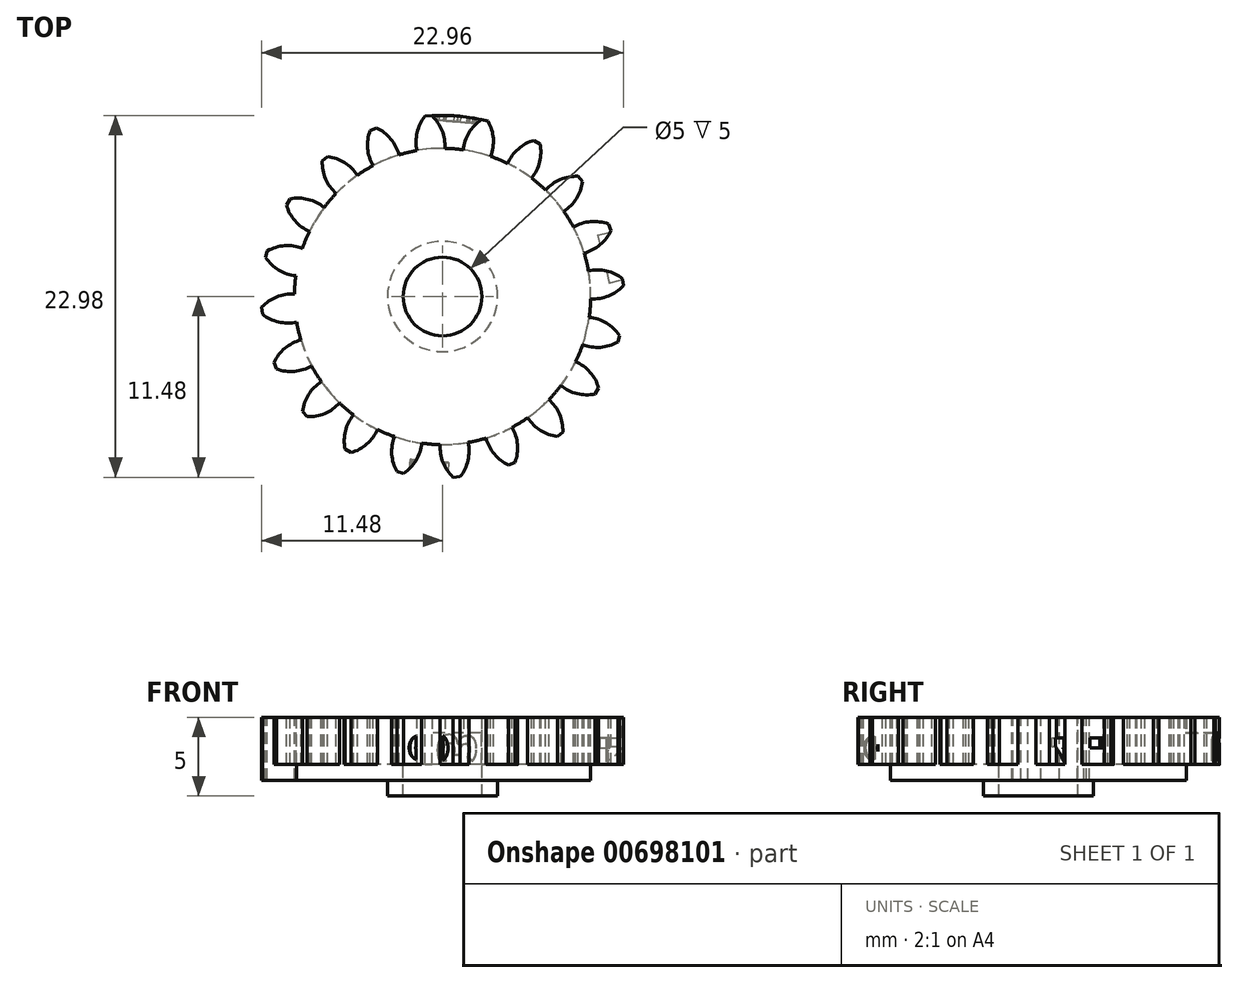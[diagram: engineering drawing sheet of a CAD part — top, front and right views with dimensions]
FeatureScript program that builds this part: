
annotation { "Feature Type Name" : "Feature", "Feature Type Description" : "" }
export const myFeature = defineFeature(function(context is Context, id is Id, definition is map)
    precondition{}
    {
        {
            assignVariable(context, id + "F0", {"name" : "GearDepth", "anyValue" : 1});
        }
        {
            var Q0;
            Q0=qCreatedBy(makeId("Top.planeOp"),FACE);
            var sketch = newSketch(context, id + "F1", { "sketchPlane" : qUnion([Q0])});
            skCircle(sketch, "E0", {"center": v(0, 0) * mm, "radius": 9.4 * mm});
            skCircle(sketch, "E1", {"center": v(0, 0) * mm, "radius": 10.45 * mm, "construction": true});
            skCircle(sketch, "E2", {"center": v(0, 0) * mm, "radius": 11.5 * mm});
            skLineSegment(sketch, "E3", {"start": v(0, 0) * mm, "end": v(0, 17.6) * mm, "construction": true});
            skLineSegment(sketch, "E4", {"start": v(0, 0) * mm, "end": v(-1.42, 18) * mm, "construction": true});
            skLineSegment(sketch, "E5", {"start": v(0, 10.45) * mm, "end": v(-10.54, 10.45) * mm, "construction": true});
            skLineSegment(sketch, "E6", {"start": v(0, 10.45) * mm, "end": v(-10.3, 6.7) * mm, "construction": true});
            skCircle(sketch, "E7", {"center": v(0, 10.45) * mm, "radius": 2.61 * mm, "construction": true});
            skCircle(sketch, "E8", {"center": v(-2.46, 9.56) * mm, "radius": 2.61 * mm, "construction": true});
            skArc(sketch, "E9", {"start": v(-4.91, 10.45) * mm, "mid": v(-4.92, 10.42) * mm, "end": v(-4.94, 10.39) * mm});
            skArc(sketch, "E10.trimOffspring", {"start": v(0.15, 9.4) * mm, "mid": v(-0.03, 10.54) * mm, "end": v(-0.68, 11.48) * mm});
            skArc(sketch, "E11.MirrorCS", {"start": v(-1.62, 9.27) * mm, "mid": v(-1.62, 10.41) * mm, "end": v(-1.12, 11.45) * mm});
            skLineSegment(sketch, "E12", {"start": v(-1.12, 11.45) * mm, "end": v(-0.68, 11.48) * mm});
            skArc(sketch, "E13.1.0", {"start": v(-2.76, 9) * mm, "mid": v(-3.29, 10.01) * mm, "end": v(-4.2, 10.7) * mm});
            skLineSegment(sketch, "E13.1.1", {"start": v(-4.6, 10.54) * mm, "end": v(-4.2, 10.7) * mm});
            skArc(sketch, "E13.1.2", {"start": v(-4.4, 8.31) * mm, "mid": v(-4.76, 9.4) * mm, "end": v(-4.6, 10.54) * mm});
            skArc(sketch, "E13.2.0", {"start": v(-5.4, 7.7) * mm, "mid": v(-6.22, 8.5) * mm, "end": v(-7.3, 8.89) * mm});
            skLineSegment(sketch, "E13.2.1", {"start": v(-7.64, 8.6) * mm, "end": v(-7.3, 8.89) * mm});
            skArc(sketch, "E13.2.2", {"start": v(-6.76, 6.54) * mm, "mid": v(-7.43, 7.47) * mm, "end": v(-7.64, 8.6) * mm});
            skArc(sketch, "E13.3.0", {"start": v(-7.52, 5.65) * mm, "mid": v(-8.54, 6.17) * mm, "end": v(-9.69, 6.2) * mm});
            skLineSegment(sketch, "E13.3.1", {"start": v(-9.92, 5.82) * mm, "end": v(-9.69, 6.2) * mm});
            skArc(sketch, "E13.3.2", {"start": v(-8.45, 4.13) * mm, "mid": v(-9.37, 4.81) * mm, "end": v(-9.92, 5.82) * mm});
            skArc(sketch, "E13.4.0", {"start": v(-8.9, 3.05) * mm, "mid": v(-10.03, 3.23) * mm, "end": v(-11.13, 2.9) * mm});
            skLineSegment(sketch, "E13.4.1", {"start": v(-11.23, 2.47) * mm, "end": v(-11.13, 2.9) * mm});
            skArc(sketch, "E13.4.2", {"start": v(-9.32, 1.32) * mm, "mid": v(-10.4, 1.68) * mm, "end": v(-11.23, 2.47) * mm});
            skArc(sketch, "E13.5.0", {"start": v(-9.4, 0.15) * mm, "mid": v(-10.54, -0.03) * mm, "end": v(-11.48, -0.68) * mm});
            skLineSegment(sketch, "E13.5.1", {"start": v(-11.45, -1.12) * mm, "end": v(-11.48, -0.68) * mm});
            skArc(sketch, "E13.5.2", {"start": v(-9.27, -1.62) * mm, "mid": v(-10.41, -1.62) * mm, "end": v(-11.45, -1.12) * mm});
            skArc(sketch, "E13.6.0", {"start": v(-9, -2.76) * mm, "mid": v(-10.01, -3.29) * mm, "end": v(-10.7, -4.2) * mm});
            skLineSegment(sketch, "E13.6.1", {"start": v(-10.54, -4.6) * mm, "end": v(-10.7, -4.2) * mm});
            skArc(sketch, "E13.6.2", {"start": v(-8.31, -4.4) * mm, "mid": v(-9.4, -4.76) * mm, "end": v(-10.54, -4.6) * mm});
            skArc(sketch, "E13.7.0", {"start": v(-7.7, -5.4) * mm, "mid": v(-8.5, -6.22) * mm, "end": v(-8.89, -7.3) * mm});
            skLineSegment(sketch, "E13.7.1", {"start": v(-8.6, -7.64) * mm, "end": v(-8.89, -7.3) * mm});
            skArc(sketch, "E13.7.2", {"start": v(-6.54, -6.76) * mm, "mid": v(-7.47, -7.43) * mm, "end": v(-8.6, -7.64) * mm});
            skArc(sketch, "E13.8.0", {"start": v(-5.65, -7.52) * mm, "mid": v(-6.17, -8.54) * mm, "end": v(-6.2, -9.69) * mm});
            skLineSegment(sketch, "E13.8.1", {"start": v(-5.82, -9.92) * mm, "end": v(-6.2, -9.69) * mm});
            skArc(sketch, "E13.8.2", {"start": v(-4.13, -8.45) * mm, "mid": v(-4.81, -9.37) * mm, "end": v(-5.82, -9.92) * mm});
            skArc(sketch, "E13.9.0", {"start": v(-3.05, -8.9) * mm, "mid": v(-3.23, -10.03) * mm, "end": v(-2.9, -11.13) * mm});
            skLineSegment(sketch, "E13.9.1", {"start": v(-2.47, -11.23) * mm, "end": v(-2.9, -11.13) * mm});
            skArc(sketch, "E13.9.2", {"start": v(-1.32, -9.32) * mm, "mid": v(-1.68, -10.4) * mm, "end": v(-2.47, -11.23) * mm});
            skArc(sketch, "E13.10.0", {"start": v(-0.15, -9.4) * mm, "mid": v(0.03, -10.54) * mm, "end": v(0.68, -11.48) * mm});
            skLineSegment(sketch, "E13.10.1", {"start": v(1.12, -11.45) * mm, "end": v(0.68, -11.48) * mm});
            skArc(sketch, "E13.10.2", {"start": v(1.62, -9.27) * mm, "mid": v(1.62, -10.41) * mm, "end": v(1.12, -11.45) * mm});
            skArc(sketch, "E13.11.0", {"start": v(2.76, -9) * mm, "mid": v(3.29, -10.01) * mm, "end": v(4.2, -10.7) * mm});
            skLineSegment(sketch, "E13.11.1", {"start": v(4.6, -10.54) * mm, "end": v(4.2, -10.7) * mm});
            skArc(sketch, "E13.11.2", {"start": v(4.4, -8.31) * mm, "mid": v(4.76, -9.4) * mm, "end": v(4.6, -10.54) * mm});
            skArc(sketch, "E13.12.0", {"start": v(5.4, -7.7) * mm, "mid": v(6.22, -8.5) * mm, "end": v(7.3, -8.89) * mm});
            skLineSegment(sketch, "E13.12.1", {"start": v(7.64, -8.6) * mm, "end": v(7.3, -8.89) * mm});
            skArc(sketch, "E13.12.2", {"start": v(6.76, -6.54) * mm, "mid": v(7.43, -7.47) * mm, "end": v(7.64, -8.6) * mm});
            skArc(sketch, "E13.13.0", {"start": v(7.52, -5.65) * mm, "mid": v(8.54, -6.17) * mm, "end": v(9.69, -6.2) * mm});
            skLineSegment(sketch, "E13.13.1", {"start": v(9.92, -5.82) * mm, "end": v(9.69, -6.2) * mm});
            skArc(sketch, "E13.13.2", {"start": v(8.45, -4.13) * mm, "mid": v(9.37, -4.81) * mm, "end": v(9.92, -5.82) * mm});
            skArc(sketch, "E13.14.0", {"start": v(8.9, -3.05) * mm, "mid": v(10.03, -3.23) * mm, "end": v(11.13, -2.9) * mm});
            skLineSegment(sketch, "E13.14.1", {"start": v(11.23, -2.47) * mm, "end": v(11.13, -2.9) * mm});
            skArc(sketch, "E13.14.2", {"start": v(9.32, -1.32) * mm, "mid": v(10.4, -1.68) * mm, "end": v(11.23, -2.47) * mm});
            skArc(sketch, "E13.15.0", {"start": v(9.4, -0.15) * mm, "mid": v(10.54, 0.03) * mm, "end": v(11.48, 0.68) * mm});
            skLineSegment(sketch, "E13.15.1", {"start": v(11.45, 1.12) * mm, "end": v(11.48, 0.68) * mm});
            skArc(sketch, "E13.15.2", {"start": v(9.27, 1.62) * mm, "mid": v(10.41, 1.62) * mm, "end": v(11.45, 1.12) * mm});
            skArc(sketch, "E13.16.0", {"start": v(9, 2.76) * mm, "mid": v(10.01, 3.29) * mm, "end": v(10.7, 4.2) * mm});
            skLineSegment(sketch, "E13.16.1", {"start": v(10.54, 4.6) * mm, "end": v(10.7, 4.2) * mm});
            skArc(sketch, "E13.16.2", {"start": v(8.31, 4.4) * mm, "mid": v(9.4, 4.76) * mm, "end": v(10.54, 4.6) * mm});
            skArc(sketch, "E13.17.0", {"start": v(7.7, 5.4) * mm, "mid": v(8.5, 6.22) * mm, "end": v(8.89, 7.3) * mm});
            skLineSegment(sketch, "E13.17.1", {"start": v(8.6, 7.64) * mm, "end": v(8.89, 7.3) * mm});
            skArc(sketch, "E13.17.2", {"start": v(6.54, 6.76) * mm, "mid": v(7.47, 7.43) * mm, "end": v(8.6, 7.64) * mm});
            skArc(sketch, "E13.18.0", {"start": v(5.65, 7.52) * mm, "mid": v(6.17, 8.54) * mm, "end": v(6.2, 9.69) * mm});
            skLineSegment(sketch, "E13.18.1", {"start": v(5.82, 9.92) * mm, "end": v(6.2, 9.69) * mm});
            skArc(sketch, "E13.18.2", {"start": v(4.13, 8.45) * mm, "mid": v(4.81, 9.37) * mm, "end": v(5.82, 9.92) * mm});
            skArc(sketch, "E13.19.0", {"start": v(3.05, 8.9) * mm, "mid": v(3.23, 10.03) * mm, "end": v(2.9, 11.13) * mm});
            skLineSegment(sketch, "E13.19.1", {"start": v(2.47, 11.23) * mm, "end": v(2.9, 11.13) * mm});
            skArc(sketch, "E13.19.2", {"start": v(1.32, 9.32) * mm, "mid": v(1.68, 10.4) * mm, "end": v(2.47, 11.23) * mm});
            skCircle(sketch, "E14", {"center": v(0, 0) * mm, "radius": 2.5 * mm});
            skCircle(sketch, "E15", {"center": v(0, 0) * mm, "radius": 3.5 * mm});
            skPoint(sketch, "E16", {"position": v(-11.47, 0.86) * mm});
            skSolve(sketch);
        }
        {
            var Q0;
            {var subQ0=sQuery(id+"F1.wireOp",EDGE,"E13.5.0");Q0=makeQuery(id+"F1.imprint","IMPRINT",FACE,{"disambiguationData":[TD([[makeQuery(id+"F1.imprint","IMPRINT",EDGE,{"derivedFrom":subQ0}),1.0]])]});}
            var Q1;
            {var subQ0=sQuery(id+"F1.wireOp",EDGE,"E13.4.0");Q1=makeQuery(id+"F1.imprint","IMPRINT",FACE,{"disambiguationData":[TD([[makeQuery(id+"F1.imprint","IMPRINT",EDGE,{"derivedFrom":subQ0}),1.0]])]});}
            var Q2;
            Q2=makeQuery(id+"F1.imprint","IMPRINT",FACE,{"disambiguationData":[TD([[makeQuery(id+"F1.imprint","IMPRINT",EDGE,{"derivedFrom":sQuery(id+"F1.wireOp",EDGE,"E14")}),-1.0]])]});
            var Q3;
            Q3=makeQuery(id+"F1.imprint","IMPRINT",FACE,{"disambiguationData":[TD([[makeQuery(id+"F1.imprint","IMPRINT",EDGE,{"derivedFrom":sQuery(id+"F1.wireOp",EDGE,"E15")}),-1.0]])]});
            extrude(context, id + "F2", {"entities" : qUnion([Q0, Q1, Q2, Q3]), "oppositeDirection" : true, "depth" : 3 * mm});
        }
        {
            var Q0;
            Q0=makeQuery(id+"F1.imprint","IMPRINT",FACE,{"disambiguationData":[TD([[makeQuery(id+"F1.imprint","IMPRINT",EDGE,{"derivedFrom":sQuery(id+"F1.wireOp",EDGE,"E14")}),-1.0]])]});
            var Q1;
            {var subQ0=sQuery(id+"F1.wireOp",EDGE,"E13.10.2");Q1=makeQuery(id+"F1.imprint","IMPRINT",FACE,{"disambiguationData":[TD([[makeQuery(id+"F1.imprint","IMPRINT",EDGE,{"derivedFrom":subQ0}),1.0]])]});}
            var Q2;
            {var subQ0=sQuery(id+"F1.wireOp",EDGE,"E13.11.0");Q2=makeQuery(id+"F1.imprint","IMPRINT",FACE,{"disambiguationData":[TD([[makeQuery(id+"F1.imprint","IMPRINT",EDGE,{"derivedFrom":subQ0}),1.0]])]});}
            var Q3;
            {var subQ0=sQuery(id+"F1.wireOp",EDGE,"E13.11.2");Q3=makeQuery(id+"F1.imprint","IMPRINT",FACE,{"disambiguationData":[TD([[makeQuery(id+"F1.imprint","IMPRINT",EDGE,{"derivedFrom":subQ0}),1.0]])]});}
            var Q4;
            {var subQ0=sQuery(id+"F1.wireOp",EDGE,"E13.12.0");Q4=makeQuery(id+"F1.imprint","IMPRINT",FACE,{"disambiguationData":[TD([[makeQuery(id+"F1.imprint","IMPRINT",EDGE,{"derivedFrom":subQ0}),1.0]])]});}
            var Q5;
            {var subQ0=sQuery(id+"F1.wireOp",EDGE,"E13.12.2");Q5=makeQuery(id+"F1.imprint","IMPRINT",FACE,{"disambiguationData":[TD([[makeQuery(id+"F1.imprint","IMPRINT",EDGE,{"derivedFrom":subQ0}),1.0]])]});}
            var Q6;
            {var subQ0=sQuery(id+"F1.wireOp",EDGE,"E13.13.0");Q6=makeQuery(id+"F1.imprint","IMPRINT",FACE,{"disambiguationData":[TD([[makeQuery(id+"F1.imprint","IMPRINT",EDGE,{"derivedFrom":subQ0}),1.0]])]});}
            var Q7;
            {var subQ0=sQuery(id+"F1.wireOp",EDGE,"E13.13.2");Q7=makeQuery(id+"F1.imprint","IMPRINT",FACE,{"disambiguationData":[TD([[makeQuery(id+"F1.imprint","IMPRINT",EDGE,{"derivedFrom":subQ0}),1.0]])]});}
            var Q8;
            {var subQ0=sQuery(id+"F1.wireOp",EDGE,"E13.14.0");Q8=makeQuery(id+"F1.imprint","IMPRINT",FACE,{"disambiguationData":[TD([[makeQuery(id+"F1.imprint","IMPRINT",EDGE,{"derivedFrom":subQ0}),1.0]])]});}
            var Q9;
            {var subQ0=sQuery(id+"F1.wireOp",EDGE,"E13.14.2");Q9=makeQuery(id+"F1.imprint","IMPRINT",FACE,{"disambiguationData":[TD([[makeQuery(id+"F1.imprint","IMPRINT",EDGE,{"derivedFrom":subQ0}),1.0]])]});}
            var Q10;
            {var subQ0=sQuery(id+"F1.wireOp",EDGE,"E13.15.0");Q10=makeQuery(id+"F1.imprint","IMPRINT",FACE,{"disambiguationData":[TD([[makeQuery(id+"F1.imprint","IMPRINT",EDGE,{"derivedFrom":subQ0}),1.0]])]});}
            var Q11;
            {var subQ0=sQuery(id+"F1.wireOp",EDGE,"E13.15.2");Q11=makeQuery(id+"F1.imprint","IMPRINT",FACE,{"disambiguationData":[TD([[makeQuery(id+"F1.imprint","IMPRINT",EDGE,{"derivedFrom":subQ0}),1.0]])]});}
            var Q12;
            {var subQ0=sQuery(id+"F1.wireOp",EDGE,"E13.16.0");Q12=makeQuery(id+"F1.imprint","IMPRINT",FACE,{"disambiguationData":[TD([[makeQuery(id+"F1.imprint","IMPRINT",EDGE,{"derivedFrom":subQ0}),1.0]])]});}
            var Q13;
            {var subQ0=sQuery(id+"F1.wireOp",EDGE,"E13.16.2");Q13=makeQuery(id+"F1.imprint","IMPRINT",FACE,{"disambiguationData":[TD([[makeQuery(id+"F1.imprint","IMPRINT",EDGE,{"derivedFrom":subQ0}),1.0]])]});}
            var Q14;
            {var subQ0=sQuery(id+"F1.wireOp",EDGE,"E13.17.0");Q14=makeQuery(id+"F1.imprint","IMPRINT",FACE,{"disambiguationData":[TD([[makeQuery(id+"F1.imprint","IMPRINT",EDGE,{"derivedFrom":subQ0}),1.0]])]});}
            var Q15;
            {var subQ0=sQuery(id+"F1.wireOp",EDGE,"E13.17.2");Q15=makeQuery(id+"F1.imprint","IMPRINT",FACE,{"disambiguationData":[TD([[makeQuery(id+"F1.imprint","IMPRINT",EDGE,{"derivedFrom":subQ0}),1.0]])]});}
            var Q16;
            {var subQ0=sQuery(id+"F1.wireOp",EDGE,"E13.18.0");Q16=makeQuery(id+"F1.imprint","IMPRINT",FACE,{"disambiguationData":[TD([[makeQuery(id+"F1.imprint","IMPRINT",EDGE,{"derivedFrom":subQ0}),1.0]])]});}
            var Q17;
            {var subQ0=sQuery(id+"F1.wireOp",EDGE,"E13.18.2");Q17=makeQuery(id+"F1.imprint","IMPRINT",FACE,{"disambiguationData":[TD([[makeQuery(id+"F1.imprint","IMPRINT",EDGE,{"derivedFrom":subQ0}),1.0]])]});}
            var Q18;
            {var subQ0=sQuery(id+"F1.wireOp",EDGE,"E13.19.0");Q18=makeQuery(id+"F1.imprint","IMPRINT",FACE,{"disambiguationData":[TD([[makeQuery(id+"F1.imprint","IMPRINT",EDGE,{"derivedFrom":subQ0}),1.0]])]});}
            var Q19;
            {var subQ0=sQuery(id+"F1.wireOp",EDGE,"E10.trimOffspring");Q19=makeQuery(id+"F1.imprint","IMPRINT",FACE,{"disambiguationData":[TD([[makeQuery(id+"F1.imprint","IMPRINT",EDGE,{"derivedFrom":subQ0}),-1.0]])]});}
            var Q20;
            {var subQ0=sQuery(id+"F1.wireOp",EDGE,"E10.trimOffspring");Q20=makeQuery(id+"F1.imprint","IMPRINT",FACE,{"disambiguationData":[TD([[makeQuery(id+"F1.imprint","IMPRINT",EDGE,{"derivedFrom":subQ0}),1.0]])]});}
            var Q21;
            {var subQ0=sQuery(id+"F1.wireOp",EDGE,"E11.MirrorCS");Q21=makeQuery(id+"F1.imprint","IMPRINT",FACE,{"disambiguationData":[TD([[makeQuery(id+"F1.imprint","IMPRINT",EDGE,{"derivedFrom":subQ0}),1.0]])]});}
            var Q22;
            {var subQ0=sQuery(id+"F1.wireOp",EDGE,"E13.1.0");Q22=makeQuery(id+"F1.imprint","IMPRINT",FACE,{"disambiguationData":[TD([[makeQuery(id+"F1.imprint","IMPRINT",EDGE,{"derivedFrom":subQ0}),1.0]])]});}
            var Q23;
            {var subQ0=sQuery(id+"F1.wireOp",EDGE,"E13.1.2");Q23=makeQuery(id+"F1.imprint","IMPRINT",FACE,{"disambiguationData":[TD([[makeQuery(id+"F1.imprint","IMPRINT",EDGE,{"derivedFrom":subQ0}),1.0]])]});}
            var Q24;
            {var subQ0=sQuery(id+"F1.wireOp",EDGE,"E13.2.0");Q24=makeQuery(id+"F1.imprint","IMPRINT",FACE,{"disambiguationData":[TD([[makeQuery(id+"F1.imprint","IMPRINT",EDGE,{"derivedFrom":subQ0}),1.0]])]});}
            var Q25;
            {var subQ0=sQuery(id+"F1.wireOp",EDGE,"E13.2.2");Q25=makeQuery(id+"F1.imprint","IMPRINT",FACE,{"disambiguationData":[TD([[makeQuery(id+"F1.imprint","IMPRINT",EDGE,{"derivedFrom":subQ0}),1.0]])]});}
            var Q26;
            {var subQ0=sQuery(id+"F1.wireOp",EDGE,"E13.3.0");Q26=makeQuery(id+"F1.imprint","IMPRINT",FACE,{"disambiguationData":[TD([[makeQuery(id+"F1.imprint","IMPRINT",EDGE,{"derivedFrom":subQ0}),1.0]])]});}
            var Q27;
            {var subQ0=sQuery(id+"F1.wireOp",EDGE,"E13.3.2");Q27=makeQuery(id+"F1.imprint","IMPRINT",FACE,{"disambiguationData":[TD([[makeQuery(id+"F1.imprint","IMPRINT",EDGE,{"derivedFrom":subQ0}),1.0]])]});}
            var Q28;
            {var subQ0=sQuery(id+"F1.wireOp",EDGE,"E13.4.0");Q28=makeQuery(id+"F1.imprint","IMPRINT",FACE,{"disambiguationData":[TD([[makeQuery(id+"F1.imprint","IMPRINT",EDGE,{"derivedFrom":subQ0}),1.0]])]});}
            var Q29;
            {var subQ0=sQuery(id+"F1.wireOp",EDGE,"E13.4.2");Q29=makeQuery(id+"F1.imprint","IMPRINT",FACE,{"disambiguationData":[TD([[makeQuery(id+"F1.imprint","IMPRINT",EDGE,{"derivedFrom":subQ0}),1.0]])]});}
            var Q30;
            {var subQ0=sQuery(id+"F1.wireOp",EDGE,"E13.5.0");Q30=makeQuery(id+"F1.imprint","IMPRINT",FACE,{"disambiguationData":[TD([[makeQuery(id+"F1.imprint","IMPRINT",EDGE,{"derivedFrom":subQ0}),1.0]])]});}
            var Q31;
            {var subQ0=sQuery(id+"F1.wireOp",EDGE,"E13.5.2");Q31=makeQuery(id+"F1.imprint","IMPRINT",FACE,{"disambiguationData":[TD([[makeQuery(id+"F1.imprint","IMPRINT",EDGE,{"derivedFrom":subQ0}),1.0]])]});}
            var Q32;
            {var subQ0=sQuery(id+"F1.wireOp",EDGE,"E13.6.0");Q32=makeQuery(id+"F1.imprint","IMPRINT",FACE,{"disambiguationData":[TD([[makeQuery(id+"F1.imprint","IMPRINT",EDGE,{"derivedFrom":subQ0}),1.0]])]});}
            var Q33;
            {var subQ0=sQuery(id+"F1.wireOp",EDGE,"E13.6.2");Q33=makeQuery(id+"F1.imprint","IMPRINT",FACE,{"disambiguationData":[TD([[makeQuery(id+"F1.imprint","IMPRINT",EDGE,{"derivedFrom":subQ0}),1.0]])]});}
            var Q34;
            {var subQ0=sQuery(id+"F1.wireOp",EDGE,"E13.7.0");Q34=makeQuery(id+"F1.imprint","IMPRINT",FACE,{"disambiguationData":[TD([[makeQuery(id+"F1.imprint","IMPRINT",EDGE,{"derivedFrom":subQ0}),1.0]])]});}
            var Q35;
            {var subQ0=sQuery(id+"F1.wireOp",EDGE,"E13.7.2");Q35=makeQuery(id+"F1.imprint","IMPRINT",FACE,{"disambiguationData":[TD([[makeQuery(id+"F1.imprint","IMPRINT",EDGE,{"derivedFrom":subQ0}),1.0]])]});}
            var Q36;
            {var subQ0=sQuery(id+"F1.wireOp",EDGE,"E13.8.0");Q36=makeQuery(id+"F1.imprint","IMPRINT",FACE,{"disambiguationData":[TD([[makeQuery(id+"F1.imprint","IMPRINT",EDGE,{"derivedFrom":subQ0}),1.0]])]});}
            var Q37;
            {var subQ0=sQuery(id+"F1.wireOp",EDGE,"E13.8.2");Q37=makeQuery(id+"F1.imprint","IMPRINT",FACE,{"disambiguationData":[TD([[makeQuery(id+"F1.imprint","IMPRINT",EDGE,{"derivedFrom":subQ0}),1.0]])]});}
            var Q38;
            {var subQ0=sQuery(id+"F1.wireOp",EDGE,"E13.9.0");Q38=makeQuery(id+"F1.imprint","IMPRINT",FACE,{"disambiguationData":[TD([[makeQuery(id+"F1.imprint","IMPRINT",EDGE,{"derivedFrom":subQ0}),1.0]])]});}
            var Q39;
            {var subQ0=sQuery(id+"F1.wireOp",EDGE,"E13.9.2");Q39=makeQuery(id+"F1.imprint","IMPRINT",FACE,{"disambiguationData":[TD([[makeQuery(id+"F1.imprint","IMPRINT",EDGE,{"derivedFrom":subQ0}),1.0]])]});}
            var Q40;
            {var subQ0=sQuery(id+"F1.wireOp",EDGE,"E13.10.0");Q40=makeQuery(id+"F1.imprint","IMPRINT",FACE,{"disambiguationData":[TD([[makeQuery(id+"F1.imprint","IMPRINT",EDGE,{"derivedFrom":subQ0}),1.0]])]});}
            var Q41;
            Q41=makeQuery(id+"F1.imprint","IMPRINT",FACE,{"disambiguationData":[TD([[makeQuery(id+"F1.imprint","IMPRINT",EDGE,{"derivedFrom":sQuery(id+"F1.wireOp",EDGE,"E15")}),-1.0]])]});
            extrude(context, id + "F3", {"entities" : qUnion([Q0, Q1, Q2, Q3, Q4, Q5, Q6, Q7, Q8, Q9, Q10, Q11, Q12, Q13, Q14, Q15, Q16, Q17, Q18, Q19, Q20, Q21, Q22, Q23, Q24, Q25, Q26, Q27, Q28, Q29, Q30, Q31, Q32, Q33, Q34, Q35, Q36, Q37, Q38, Q39, Q40, Q41]), "operationType" : NewBodyOperationType.ADD, "oppositeDirection" : true, "depth" : 2 * mm});
        }
        {
            var Q0;
            {var subQ0=sQuery(id+"F1.wireOp",EDGE,"E10.trimOffspring");Q0=makeQuery(id+"F1.imprint","IMPRINT",FACE,{"disambiguationData":[TD([[makeQuery(id+"F1.imprint","IMPRINT",EDGE,{"derivedFrom":subQ0}),1.0]])]});}
            var Q1;
            {var subQ0=sQuery(id+"F1.wireOp",EDGE,"E0");var subQ1=makeQuery(id+"F1.imprint","INTERSECT",VERTEX,{"derivedFrom":[subQ0,sQuery(id+"F1.wireOp",EDGE,"E10.trimOffspring")]});Q1=makeQuery(id+"F1.imprint","IMPRINT",FACE,{"disambiguationData":[TD([[makeQuery(id+"F1.imprint","IMPRINT",EDGE,{"disambiguationData":[TD([[subQ1,-1.0]])],"derivedFrom":subQ0}),1.0]])]});}
            var Q2;
            {var subQ0=sQuery(id+"F1.wireOp",EDGE,"E13.1.0");Q2=makeQuery(id+"F1.imprint","IMPRINT",FACE,{"disambiguationData":[TD([[makeQuery(id+"F1.imprint","IMPRINT",EDGE,{"derivedFrom":subQ0}),1.0]])]});}
            var Q3;
            {var subQ0=sQuery(id+"F1.wireOp",EDGE,"E13.2.0");Q3=makeQuery(id+"F1.imprint","IMPRINT",FACE,{"disambiguationData":[TD([[makeQuery(id+"F1.imprint","IMPRINT",EDGE,{"derivedFrom":subQ0}),1.0]])]});}
            var Q4;
            {var subQ0=sQuery(id+"F1.wireOp",EDGE,"E13.3.0");Q4=makeQuery(id+"F1.imprint","IMPRINT",FACE,{"disambiguationData":[TD([[makeQuery(id+"F1.imprint","IMPRINT",EDGE,{"derivedFrom":subQ0}),1.0]])]});}
            var Q5;
            {var subQ0=sQuery(id+"F1.wireOp",EDGE,"E13.4.0");Q5=makeQuery(id+"F1.imprint","IMPRINT",FACE,{"disambiguationData":[TD([[makeQuery(id+"F1.imprint","IMPRINT",EDGE,{"derivedFrom":subQ0}),1.0]])]});}
            var Q6;
            {var subQ0=sQuery(id+"F1.wireOp",EDGE,"E13.5.0");Q6=makeQuery(id+"F1.imprint","IMPRINT",FACE,{"disambiguationData":[TD([[makeQuery(id+"F1.imprint","IMPRINT",EDGE,{"derivedFrom":subQ0}),1.0]])]});}
            var Q7;
            {var subQ0=sQuery(id+"F1.wireOp",EDGE,"E13.6.0");Q7=makeQuery(id+"F1.imprint","IMPRINT",FACE,{"disambiguationData":[TD([[makeQuery(id+"F1.imprint","IMPRINT",EDGE,{"derivedFrom":subQ0}),1.0]])]});}
            var Q8;
            {var subQ0=sQuery(id+"F1.wireOp",EDGE,"E13.7.0");Q8=makeQuery(id+"F1.imprint","IMPRINT",FACE,{"disambiguationData":[TD([[makeQuery(id+"F1.imprint","IMPRINT",EDGE,{"derivedFrom":subQ0}),1.0]])]});}
            var Q9;
            {var subQ0=sQuery(id+"F1.wireOp",EDGE,"E13.8.0");Q9=makeQuery(id+"F1.imprint","IMPRINT",FACE,{"disambiguationData":[TD([[makeQuery(id+"F1.imprint","IMPRINT",EDGE,{"derivedFrom":subQ0}),1.0]])]});}
            var Q10;
            {var subQ0=sQuery(id+"F1.wireOp",EDGE,"E13.9.0");Q10=makeQuery(id+"F1.imprint","IMPRINT",FACE,{"disambiguationData":[TD([[makeQuery(id+"F1.imprint","IMPRINT",EDGE,{"derivedFrom":subQ0}),1.0]])]});}
            var Q11;
            {var subQ0=sQuery(id+"F1.wireOp",EDGE,"E13.10.0");Q11=makeQuery(id+"F1.imprint","IMPRINT",FACE,{"disambiguationData":[TD([[makeQuery(id+"F1.imprint","IMPRINT",EDGE,{"derivedFrom":subQ0}),1.0]])]});}
            var Q12;
            {var subQ0=sQuery(id+"F1.wireOp",EDGE,"E13.11.0");Q12=makeQuery(id+"F1.imprint","IMPRINT",FACE,{"disambiguationData":[TD([[makeQuery(id+"F1.imprint","IMPRINT",EDGE,{"derivedFrom":subQ0}),1.0]])]});}
            var Q13;
            {var subQ0=sQuery(id+"F1.wireOp",EDGE,"E13.12.0");Q13=makeQuery(id+"F1.imprint","IMPRINT",FACE,{"disambiguationData":[TD([[makeQuery(id+"F1.imprint","IMPRINT",EDGE,{"derivedFrom":subQ0}),1.0]])]});}
            var Q14;
            {var subQ0=sQuery(id+"F1.wireOp",EDGE,"E13.13.0");Q14=makeQuery(id+"F1.imprint","IMPRINT",FACE,{"disambiguationData":[TD([[makeQuery(id+"F1.imprint","IMPRINT",EDGE,{"derivedFrom":subQ0}),1.0]])]});}
            var Q15;
            {var subQ0=sQuery(id+"F1.wireOp",EDGE,"E13.14.0");Q15=makeQuery(id+"F1.imprint","IMPRINT",FACE,{"disambiguationData":[TD([[makeQuery(id+"F1.imprint","IMPRINT",EDGE,{"derivedFrom":subQ0}),1.0]])]});}
            var Q16;
            {var subQ0=sQuery(id+"F1.wireOp",EDGE,"E13.15.0");Q16=makeQuery(id+"F1.imprint","IMPRINT",FACE,{"disambiguationData":[TD([[makeQuery(id+"F1.imprint","IMPRINT",EDGE,{"derivedFrom":subQ0}),1.0]])]});}
            var Q17;
            {var subQ0=sQuery(id+"F1.wireOp",EDGE,"E13.16.0");Q17=makeQuery(id+"F1.imprint","IMPRINT",FACE,{"disambiguationData":[TD([[makeQuery(id+"F1.imprint","IMPRINT",EDGE,{"derivedFrom":subQ0}),1.0]])]});}
            var Q18;
            {var subQ0=sQuery(id+"F1.wireOp",EDGE,"E13.17.0");Q18=makeQuery(id+"F1.imprint","IMPRINT",FACE,{"disambiguationData":[TD([[makeQuery(id+"F1.imprint","IMPRINT",EDGE,{"derivedFrom":subQ0}),1.0]])]});}
            var Q19;
            {var subQ0=sQuery(id+"F1.wireOp",EDGE,"E13.18.0");Q19=makeQuery(id+"F1.imprint","IMPRINT",FACE,{"disambiguationData":[TD([[makeQuery(id+"F1.imprint","IMPRINT",EDGE,{"derivedFrom":subQ0}),1.0]])]});}
            var Q20;
            {var subQ0=sQuery(id+"F1.wireOp",EDGE,"E13.19.0");Q20=makeQuery(id+"F1.imprint","IMPRINT",FACE,{"disambiguationData":[TD([[makeQuery(id+"F1.imprint","IMPRINT",EDGE,{"derivedFrom":subQ0}),1.0]])]});}
            var Q21;
            Q21=makeQuery(id+"F1.imprint","IMPRINT",FACE,{"disambiguationData":[TD([[makeQuery(id+"F1.imprint","IMPRINT",EDGE,{"derivedFrom":sQuery(id+"F1.wireOp",EDGE,"E14")}),-1.0]])]});
            var Q22;
            Q22=sQuery(id+"F1.wireOp",EDGE,"E0");
            var Q23;
            Q23=sQuery(id+"F1.wireOp",EDGE,"E10.trimOffspring");
            var Q24;
            Q24=sQuery(id+"F1.wireOp",EDGE,"E12");
            var Q25;
            Q25=sQuery(id+"F1.wireOp",EDGE,"E11.MirrorCS");
            extrude(context, id + "F4", {"entities" : qUnion([Q0, Q1, Q2, Q3, Q4, Q5, Q6, Q7, Q8, Q9, Q10, Q11, Q12, Q13, Q14, Q15, Q16, Q17, Q18, Q19, Q20, Q21]), "operationType" : NewBodyOperationType.ADD, "surfaceEntities" : qUnion([Q22, Q23, Q24, Q25]), "depth" : (getVariable(context, 'GearDepth')) * mm});
        }
        {
            assignVariable(context, id + "F5", {"name" : "FontWidth", "anyValue" : 1.8});
        }
        {
            assignVariable(context, id + "F6", {"name" : "FontDepth", "anyValue" : .5});
        }
        {
            var Q0;
            Q0=makeQuery(id+"F3.opExtrude","SWEPT_EDGE",EDGE,{"disambiguationData":[OSD([sQuery(id+"F1.wireOp",EDGE,"E2"),sQuery(id+"F1.wireOp",EDGE,"E13.3.1"),sQuery(id+"F1.wireOp",EDGE,"E13.3.2")])]});
            var Q1;
            {var subQ0=sQuery(id+"F1.wireOp",EDGE,"E13.4.1");var subQ1=sQuery(id+"F1.wireOp",EDGE,"E13.4.0");var subQ2=sQuery(id+"F1.wireOp",EDGE,"E2");Q1=makeQuery(id+"F3.boolean.opBoolean","MERGE",EDGE,{"derivedFrom":[makeQuery(id+"F2.opExtrude","SWEPT_EDGE",EDGE,{"disambiguationData":[OSD([subQ2,subQ1,subQ0])]}),makeQuery(id+"F3.opExtrude","SWEPT_EDGE",EDGE,{"disambiguationData":[OSD([subQ2,subQ1,subQ0])]})]});}
            cPlane(context, id + "F7", {"entities" : qUnion([Q0, Q1]), "cplaneType" : CPlaneType.LINE_ANGLE, "offset" : 150 * mm, "angle" : 180 * degree, "width" : 150 * mm, "height" : 150 * mm});
        }
        {
            var Q0;
            Q0=qCreatedBy(id+"F7.planeOp",FACE);
            var sketch = newSketch(context, id + "F8", { "sketchPlane" : qUnion([Q0])});
            skText(sketch, "E17", { "text": "5", "fontName": "OpenSans-Bold.ttf"});
            skLineSegment(sketch, "E18", {"start": v(-0.48, -1.07) * mm, "end": v(0.42, -1.07) * mm, "construction": true});
            const initialGuessF8  = {"E17": [0.00118, -0.001, 0, 1, 0.0011]};
            skSetInitialGuess(sketch, initialGuessF8);
            skSolve(sketch);
        }
        {
            var Q0;
            Q0=qSketchRegion(id+"F8",true);
            extrude(context, id + "F9", {"entities" : qUnion([Q0]), "operationType" : NewBodyOperationType.REMOVE, "endBound" : BoundingType.SYMMETRIC, "oppositeDirection" : true, "depth" : (getVariable(context, 'FontDepth')) * mm});
        }
        {
            var Q0;
            Q0=makeQuery(id+"F3.opExtrude","SWEPT_EDGE",EDGE,{"disambiguationData":[OSD([sQuery(id+"F1.wireOp",EDGE,"E2"),sQuery(id+"F1.wireOp",EDGE,"E13.1.1"),sQuery(id+"F1.wireOp",EDGE,"E13.1.2")])]});
            var Q1;
            Q1=makeQuery(id+"F3.opExtrude","SWEPT_EDGE",EDGE,{"disambiguationData":[OSD([sQuery(id+"F1.wireOp",EDGE,"E2"),sQuery(id+"F1.wireOp",EDGE,"E13.2.0"),sQuery(id+"F1.wireOp",EDGE,"E13.2.1")])]});
            cPlane(context, id + "F10", {"entities" : qUnion([Q0, Q1]), "cplaneType" : CPlaneType.LINE_ANGLE, "offset" : 150 * mm, "angle" : 180 * degree, "width" : 150 * mm, "height" : 150 * mm});
        }
        {
            var Q0;
            Q0=qCreatedBy(id+"F10.planeOp",FACE);
            var sketch = newSketch(context, id + "F11", { "sketchPlane" : qUnion([Q0])});
            skText(sketch, "E19", { "text": "4", "fontName": "OpenSans-Bold.ttf"});
            const initialGuessF11  = {"E19": [0.00118, -0.0016, 0, 1, 0.00233]};
            skSetInitialGuess(sketch, initialGuessF11);
            skSolve(sketch);
        }
        {
            var Q0;
            Q0=qSketchRegion(id+"F11",true);
            extrude(context, id + "F12", {"entities" : qUnion([Q0]), "operationType" : NewBodyOperationType.REMOVE, "endBound" : BoundingType.SYMMETRIC, "oppositeDirection" : true, "depth" : (getVariable(context, 'FontDepth')) * mm});
        }
        {
            var Q0;
            Q0=makeQuery(id+"F3.opExtrude","SWEPT_EDGE",EDGE,{"disambiguationData":[OSD([sQuery(id+"F1.wireOp",EDGE,"E2"),sQuery(id+"F1.wireOp",EDGE,"E13.19.1"),sQuery(id+"F1.wireOp",EDGE,"E13.19.2")])]});
            var Q1;
            Q1=makeQuery(id+"F3.opExtrude","SWEPT_EDGE",EDGE,{"disambiguationData":[OSD([sQuery(id+"F1.wireOp",EDGE,"E2"),sQuery(id+"F1.wireOp",EDGE,"E10.trimOffspring"),sQuery(id+"F1.wireOp",EDGE,"E12")])]});
            cPlane(context, id + "F13", {"entities" : qUnion([Q0, Q1]), "cplaneType" : CPlaneType.LINE_ANGLE, "offset" : 150 * mm, "angle" : 180 * degree, "width" : 150 * mm, "height" : 150 * mm});
        }
        {
            var Q0;
            Q0=qCreatedBy(id+"F13.planeOp",FACE);
            var sketch = newSketch(context, id + "F14", { "sketchPlane" : qUnion([Q0])});
            skText(sketch, "E20", { "text": "3", "fontName": "OpenSans-Bold.ttf"});
            const initialGuessF14  = {"E20": [0.00118, -0.0019, 0, 1, 0.00244]};
            skSetInitialGuess(sketch, initialGuessF14);
            skSolve(sketch);
        }
        {
            var Q0;
            Q0=qSketchRegion(id+"F14",true);
            extrude(context, id + "F15", {"entities" : qUnion([Q0]), "operationType" : NewBodyOperationType.REMOVE, "endBound" : BoundingType.SYMMETRIC, "oppositeDirection" : true, "depth" : (getVariable(context, 'FontDepth')) * mm});
        }
        {
            var Q0;
            Q0=makeQuery(id+"F3.opExtrude","SWEPT_EDGE",EDGE,{"disambiguationData":[OSD([sQuery(id+"F1.wireOp",EDGE,"E2"),sQuery(id+"F1.wireOp",EDGE,"E13.17.1"),sQuery(id+"F1.wireOp",EDGE,"E13.17.2")])]});
            var Q1;
            Q1=makeQuery(id+"F3.opExtrude","SWEPT_EDGE",EDGE,{"disambiguationData":[OSD([sQuery(id+"F1.wireOp",EDGE,"E2"),sQuery(id+"F1.wireOp",EDGE,"E13.18.0"),sQuery(id+"F1.wireOp",EDGE,"E13.18.1")])]});
            cPlane(context, id + "F16", {"entities" : qUnion([Q0, Q1]), "cplaneType" : CPlaneType.LINE_ANGLE, "offset" : 150 * mm, "angle" : 180 * degree, "width" : 150 * mm, "height" : 150 * mm});
        }
        {
            var Q0;
            Q0=qCreatedBy(id+"F16.planeOp",FACE);
            var sketch = newSketch(context, id + "F17", { "sketchPlane" : qUnion([Q0])});
            skText(sketch, "E21", { "text": "2", "fontName": "OpenSans-Bold.ttf"});
            const initialGuessF17  = {"E21": [0.00118, -0.0019, 0, 1, 0.0024]};
            skSetInitialGuess(sketch, initialGuessF17);
            skSolve(sketch);
        }
        {
            var Q0;
            Q0=qSketchRegion(id+"F17",true);
            extrude(context, id + "F18", {"entities" : qUnion([Q0]), "operationType" : NewBodyOperationType.REMOVE, "endBound" : BoundingType.SYMMETRIC, "depth" : (getVariable(context, 'FontDepth')) * mm});
        }
        {
            var Q0;
            Q0=makeQuery(id+"F3.opExtrude","SWEPT_EDGE",EDGE,{"disambiguationData":[OSD([sQuery(id+"F1.wireOp",EDGE,"E2"),sQuery(id+"F1.wireOp",EDGE,"E13.15.1"),sQuery(id+"F1.wireOp",EDGE,"E13.15.2")])]});
            var Q1;
            Q1=makeQuery(id+"F3.opExtrude","SWEPT_EDGE",EDGE,{"disambiguationData":[OSD([sQuery(id+"F1.wireOp",EDGE,"E2"),sQuery(id+"F1.wireOp",EDGE,"E13.16.0"),sQuery(id+"F1.wireOp",EDGE,"E13.16.1")])]});
            cPlane(context, id + "F19", {"entities" : qUnion([Q0, Q1]), "cplaneType" : CPlaneType.LINE_ANGLE, "offset" : 150 * mm, "angle" : 180 * degree, "width" : 150 * mm, "height" : 150 * mm});
        }
        {
            var Q0;
            Q0=qCreatedBy(id+"F19.planeOp",FACE);
            var sketch = newSketch(context, id + "F20", { "sketchPlane" : qUnion([Q0])});
            skText(sketch, "E22", { "text": "1", "fontName": "OpenSans-Bold.ttf"});
            const initialGuessF20  = {"E22": [0.00148, -0.0021, 0, 1, 0.00314]};
            skSetInitialGuess(sketch, initialGuessF20);
            skSolve(sketch);
        }
        {
            var Q0;
            Q0=qSketchRegion(id+"F20",true);
            extrude(context, id + "F21", {"entities" : qUnion([Q0]), "operationType" : NewBodyOperationType.REMOVE, "endBound" : BoundingType.SYMMETRIC, "oppositeDirection" : true, "depth" : (getVariable(context, 'FontWidth')) * mm});
        }
        {
            var Q0;
            Q0=makeQuery(id+"F3.opExtrude","SWEPT_EDGE",EDGE,{"disambiguationData":[OSD([sQuery(id+"F1.wireOp",EDGE,"E2"),sQuery(id+"F1.wireOp",EDGE,"E13.13.1"),sQuery(id+"F1.wireOp",EDGE,"E13.13.2")])]});
            var Q1;
            Q1=makeQuery(id+"F3.opExtrude","SWEPT_EDGE",EDGE,{"disambiguationData":[OSD([sQuery(id+"F1.wireOp",EDGE,"E2"),sQuery(id+"F1.wireOp",EDGE,"E13.14.0"),sQuery(id+"F1.wireOp",EDGE,"E13.14.1")])]});
            cPlane(context, id + "F22", {"entities" : qUnion([Q0, Q1]), "cplaneType" : CPlaneType.LINE_ANGLE, "offset" : 150 * mm, "angle" : 180 * degree, "width" : 150 * mm, "height" : 150 * mm});
        }
        {
            var Q0;
            Q0=qCreatedBy(id+"F22.planeOp",FACE);
            var sketch = newSketch(context, id + "F23", { "sketchPlane" : qUnion([Q0])});
            skText(sketch, "E23", { "text": "0", "fontName": "OpenSans-Bold.ttf"});
            const initialGuessF23  = {"E23": [0.00118, -0.0019, 0, 1, 0.00242]};
            skSetInitialGuess(sketch, initialGuessF23);
            skSolve(sketch);
        }
        {
            var Q0;
            Q0=qSketchRegion(id+"F23",true);
            extrude(context, id + "F24", {"entities" : qUnion([Q0]), "operationType" : NewBodyOperationType.REMOVE, "endBound" : BoundingType.SYMMETRIC, "oppositeDirection" : true, "depth" : (getVariable(context, 'FontDepth')) * mm});
        }
        {
            var Q0;
            Q0=makeQuery(id+"F3.opExtrude","SWEPT_EDGE",EDGE,{"disambiguationData":[OSD([sQuery(id+"F1.wireOp",EDGE,"E2"),sQuery(id+"F1.wireOp",EDGE,"E13.11.1"),sQuery(id+"F1.wireOp",EDGE,"E13.11.2")])]});
            var Q1;
            Q1=makeQuery(id+"F3.opExtrude","SWEPT_EDGE",EDGE,{"disambiguationData":[OSD([sQuery(id+"F1.wireOp",EDGE,"E2"),sQuery(id+"F1.wireOp",EDGE,"E13.12.0"),sQuery(id+"F1.wireOp",EDGE,"E13.12.1")])]});
            cPlane(context, id + "F25", {"entities" : qUnion([Q0, Q1]), "cplaneType" : CPlaneType.LINE_ANGLE, "offset" : 150 * mm, "angle" : 180 * degree, "width" : 150 * mm, "height" : 150 * mm});
        }
        {
            var Q0;
            Q0=qCreatedBy(id+"F25.planeOp",FACE);
            var sketch = newSketch(context, id + "F26", { "sketchPlane" : qUnion([Q0])});
            skText(sketch, "E24", { "text": "9", "fontName": "OpenSans-Regular.ttf"});
            const initialGuessF26  = {"E24": [0.00118, -0.0019, 0, 1, 0.0025]};
            skSetInitialGuess(sketch, initialGuessF26);
            skSolve(sketch);
        }
        {
            var Q0;
            Q0=qSketchRegion(id+"F26",true);
            extrude(context, id + "F27", {"entities" : qUnion([Q0]), "operationType" : NewBodyOperationType.REMOVE, "endBound" : BoundingType.SYMMETRIC, "oppositeDirection" : true, "depth" : (getVariable(context, 'FontDepth')) * mm});
        }
        {
            var Q0;
            Q0=makeQuery(id+"F3.opExtrude","SWEPT_EDGE",EDGE,{"disambiguationData":[OSD([sQuery(id+"F1.wireOp",EDGE,"E2"),sQuery(id+"F1.wireOp",EDGE,"E13.9.1"),sQuery(id+"F1.wireOp",EDGE,"E13.9.2")])]});
            var Q1;
            Q1=makeQuery(id+"F3.opExtrude","SWEPT_EDGE",EDGE,{"disambiguationData":[OSD([sQuery(id+"F1.wireOp",EDGE,"E2"),sQuery(id+"F1.wireOp",EDGE,"E13.10.0"),sQuery(id+"F1.wireOp",EDGE,"E13.10.1")])]});
            cPlane(context, id + "F28", {"entities" : qUnion([Q0, Q1]), "cplaneType" : CPlaneType.LINE_ANGLE, "offset" : 150 * mm, "angle" : 180 * degree, "width" : 150 * mm, "height" : 150 * mm});
        }
        {
            var Q0;
            Q0=qCreatedBy(id+"F28.planeOp",FACE);
            var sketch = newSketch(context, id + "F29", { "sketchPlane" : qUnion([Q0])});
            skText(sketch, "E25", { "text": "8\n", "fontName": "OpenSans-Bold.ttf"});
            const initialGuessF29  = {"E25": [0.00118, -0.0019, 0, 1, 0.00242]};
            skSetInitialGuess(sketch, initialGuessF29);
            skSolve(sketch);
        }
        {
            var Q0;
            Q0=qSketchRegion(id+"F29",true);
            extrude(context, id + "F30", {"entities" : qUnion([Q0]), "operationType" : NewBodyOperationType.REMOVE, "endBound" : BoundingType.SYMMETRIC, "oppositeDirection" : true, "depth" : (getVariable(context, 'FontWidth')) * mm});
        }
        {
            var Q0;
            Q0=makeQuery(id+"F3.opExtrude","SWEPT_EDGE",EDGE,{"disambiguationData":[OSD([sQuery(id+"F1.wireOp",EDGE,"E2"),sQuery(id+"F1.wireOp",EDGE,"E13.7.1"),sQuery(id+"F1.wireOp",EDGE,"E13.7.2")])]});
            var Q1;
            Q1=makeQuery(id+"F3.opExtrude","SWEPT_EDGE",EDGE,{"disambiguationData":[OSD([sQuery(id+"F1.wireOp",EDGE,"E2"),sQuery(id+"F1.wireOp",EDGE,"E13.8.0"),sQuery(id+"F1.wireOp",EDGE,"E13.8.1")])]});
            cPlane(context, id + "F31", {"entities" : qUnion([Q0, Q1]), "cplaneType" : CPlaneType.LINE_ANGLE, "offset" : 150 * mm, "angle" : 180 * degree, "width" : 150 * mm, "height" : 150 * mm});
        }
        {
            var Q0;
            Q0=qCreatedBy(id+"F31.planeOp",FACE);
            var sketch = newSketch(context, id + "F32", { "sketchPlane" : qUnion([Q0])});
            skText(sketch, "E26", { "text": "7", "fontName": "OpenSans-Bold.ttf"});
            const initialGuessF32  = {"E26": [0.00118, -0.0019, 0, 1, 0.0024]};
            skSetInitialGuess(sketch, initialGuessF32);
            skSolve(sketch);
        }
        {
            var Q0;
            Q0=qSketchRegion(id+"F32",true);
            extrude(context, id + "F33", {"entities" : qUnion([Q0]), "operationType" : NewBodyOperationType.REMOVE, "endBound" : BoundingType.SYMMETRIC, "oppositeDirection" : true, "depth" : (getVariable(context, 'FontDepth')) * mm});
        }
        {
            var Q0;
            {var subQ0=sQuery(id+"F1.wireOp",EDGE,"E13.5.2");var subQ1=sQuery(id+"F1.wireOp",EDGE,"E13.5.1");var subQ2=sQuery(id+"F1.wireOp",EDGE,"E2");Q0=makeQuery(id+"F3.boolean.opBoolean","MERGE",EDGE,{"derivedFrom":[makeQuery(id+"F2.opExtrude","SWEPT_EDGE",EDGE,{"disambiguationData":[OSD([subQ2,subQ1,subQ0])]}),makeQuery(id+"F3.opExtrude","SWEPT_EDGE",EDGE,{"disambiguationData":[OSD([subQ2,subQ1,subQ0])]})]});}
            var Q1;
            Q1=makeQuery(id+"F3.opExtrude","SWEPT_EDGE",EDGE,{"disambiguationData":[OSD([sQuery(id+"F1.wireOp",EDGE,"E2"),sQuery(id+"F1.wireOp",EDGE,"E13.6.0"),sQuery(id+"F1.wireOp",EDGE,"E13.6.1")])]});
            cPlane(context, id + "F34", {"entities" : qUnion([Q0, Q1]), "cplaneType" : CPlaneType.LINE_ANGLE, "offset" : 150 * mm, "angle" : 180 * degree, "width" : 150 * mm, "height" : 150 * mm});
        }
        {
            var Q0;
            Q0=qCreatedBy(id+"F34.planeOp",FACE);
            var sketch = newSketch(context, id + "F35", { "sketchPlane" : qUnion([Q0])});
            skText(sketch, "E27", { "text": "6", "fontName": "OpenSans-Bold.ttf"});
            const initialGuessF35  = {"E27": [0.00118, -0.0019, 0, 1, 0.0024]};
            skSetInitialGuess(sketch, initialGuessF35);
            skSolve(sketch);
        }
        {
            var Q0;
            Q0=qSketchRegion(id+"F35",true);
            extrude(context, id + "F36", {"entities" : qUnion([Q0]), "operationType" : NewBodyOperationType.REMOVE, "endBound" : BoundingType.SYMMETRIC, "oppositeDirection" : true, "depth" : (getVariable(context, 'FontDepth')) * mm});
        }
        {
            var Q0;
            Q0=makeQuery(id+"F2.opExtrude","CAP_FACE",FACE,{"disambiguationData":[OSD([sQuery(id+"F1.wireOp",EDGE,"E0"),sQuery(id+"F1.wireOp",EDGE,"E13.4.0"),sQuery(id+"F1.wireOp",EDGE,"E13.4.1"),sQuery(id+"F1.wireOp",EDGE,"E13.4.2"),sQuery(id+"F1.wireOp",EDGE,"E13.5.0"),sQuery(id+"F1.wireOp",EDGE,"E13.5.1"),sQuery(id+"F1.wireOp",EDGE,"E13.5.2"),sQuery(id+"F1.wireOp",EDGE,"E14")])],"isStart":false});
            var sketch = newSketch(context, id + "F37", { "sketchPlane" : qUnion([Q0])});
            skCircle(sketch, "E28", {"center": v(0, 0) * mm, "radius": 3.5 * mm});
            skSolve(sketch);
        }
        {
            var Q0;
            Q0=makeQuery(id+"F37.imprint","IMPRINT",FACE,{"disambiguationData":[TD([[makeQuery(id+"F37.imprint","IMPRINT",EDGE,{"derivedFrom":sQuery(id+"F37.wireOp",EDGE,"E28")}),1.0]])]});
            extrude(context, id + "F38", {"entities" : qUnion([Q0]), "operationType" : NewBodyOperationType.ADD, "depth" : 1 * mm, "offsetDistance" : 25 * mm});
        }
    });
